# Revit family: 304_Green_1 A-_
name_source: partatom
category: Pipe Accessories
units: mm (PartAtom-declared; Revit-internal decimal feet)

## family parameters
Always vertical = Yes
Cut with Voids When Loaded = No
Part Type = Valve - Breaks Into
Round Connector Dimension = Use Diameter
Shared = No
Work Plane-Based = No

## types (3) — shared parameters
Description = Green.1 - Pressure Independent Control Valve
L2D_Min = 3048 mm  [stored 10 ft]
L4 = 11 mm  [stored 0.0360892 ft]
LA = 75 mm  [stored 0.246063 ft]
Manufacturer = FlowCon
QmdConnectorList = 301;D;302;D
RA = 30 mm  [stored 0.0984252 ft]
URL = http://flowcon.com
magiPartTypeId = 304
magiProductFamilyId = Green.1 A-*
zero-valued in all types: MC_Default_elevation

## per-type parameters (varying)
| type | CenSd_RN_6 | CenSd_SW_6 | D | H11 | H12 | L1 | L1__ve | L2 | L2D | L3 | L3__ve | L5 | LL | R1 | R2 | RN | SW | W2D | magiProductId |
| G.1.22.04 | 9 mm | 12 mm  [stored 0.0393701 ft] | 15 mm | 25 mm  [stored 0.082021 ft] | 54 mm | 16 mm  [stored 0.0524934 ft] | -16 mm  [stored -0.0524934 ft] | 48 mm  [stored 0.15748 ft] | 80 mm | 62 mm | -62 mm | 31 mm | 40 mm  [stored 0.131234 ft] | 11 mm  [stored 0.0360892 ft] | 13 mm | 10 mm  [stored 0.0328084 ft] | 14 mm  [stored 0.0459318 ft] | 15 mm  [stored 0.0492126 ft] | Green.1 A-15 |
| G.1.22.06 | 11 mm  [stored 0.0360892 ft] | 16 mm  [stored 0.0524934 ft] | 25 mm | 23 mm | 52 mm | 18 mm  [stored 0.0590551 ft] | -18 mm | 55 mm | 91 mm | 60 mm  [stored 0.19685 ft] | -60 mm | 30 mm  [stored 0.0984252 ft] | 46 mm | 14 mm  [stored 0.0459318 ft] | 16 mm  [stored 0.0524934 ft] | 13 mm | 18 mm  [stored 0.0590551 ft] | 25 mm  [stored 0.082021 ft] | Green.1 A-25 |
| G.1.22.05 | 10 mm  [stored 0.0328084 ft] | 14 mm  [stored 0.0459318 ft] | 20 mm | 24 mm  [stored 0.0787402 ft] | 53 mm | 16 mm  [stored 0.0524934 ft] | -16 mm  [stored -0.0524934 ft] | 48 mm  [stored 0.15748 ft] | 80 mm | 61 mm | -61 mm | 31 mm | 40 mm  [stored 0.131234 ft] | 12 mm  [stored 0.0393701 ft] | 14 mm  [stored 0.0459318 ft] | 12 mm  [stored 0.0393701 ft] | 16 mm  [stored 0.0524934 ft] | 20 mm  [stored 0.0656168 ft] | Green.1 A-20 |

note: column(s) folded — value = type name in every type: magiProductCode

note: [stored X ft] marks values corroborated as IEEE doubles in the binary element streams (Revit-internal decimal feet)

## geometry (parser evidence)
native form markers: Sweep x2
no freeform markers — native parametric forms only
